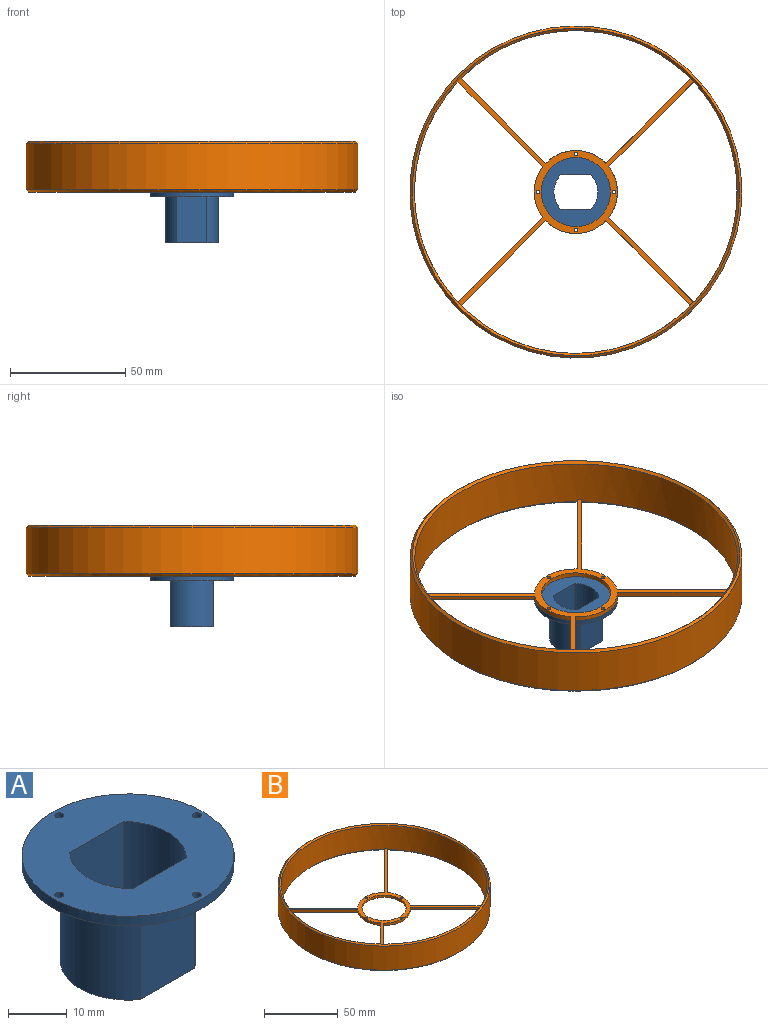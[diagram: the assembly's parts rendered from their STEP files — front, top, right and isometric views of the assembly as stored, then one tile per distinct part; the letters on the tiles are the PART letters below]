
ASSEMBLY  parts=2 mates=1
PART A: 16 faces, bbox 36x36x22 mm
  f0: plane 23x19mm, normal (0,0,-1), area 123.6mm2, adj f1,f2,f3,f8,f11,f12,f13,f14
  f1: cylinder r=10.88mm len=22mm, axis (0,0,-1), area 364.1mm2, adj f0,f2,f8,f10
  f2: plane 22x13mm, normal (0,1,0), area 286mm2, adj f0,f1,f3,f10
  f3: cylinder r=10.88mm len=22mm, axis (0,0,-1), area 364.1mm2, adj f0,f2,f8,f10
  f4: cylinder r=0.75mm len=2mm, axis (0,0,-1), area 9.4mm2, adj f10,f15
  f5: cylinder r=0.75mm len=2mm, axis (0,0,-1), area 9.4mm2, adj f10,f15
  f6: cylinder r=0.75mm len=2mm, axis (0,0,-1), area 9.4mm2, adj f10,f15
  f7: cylinder r=0.75mm len=2mm, axis (0,0,-1), area 9.4mm2, adj f10,f15
  f8: plane 22x13mm, normal (0,-1,0), area 286mm2, adj f0,f1,f3,f10
  f9: cylinder r=18mm len=36mm, axis (0,0,-1), area 226.2mm2, adj f10,f15
  f10: plane 36x36mm, normal (0,0,1), area 753.9mm2, adj f1,f2,f3,f4,f5,f6,f7,f8
  f11: plane 20x13mm, normal (0,-1,0), area 260mm2, adj f0,f12,f14,f15
  f12: cylinder r=11.53mm len=20mm, axis (0,0,-1), area 446.7mm2, adj f0,f11,f13,f15
  f13: plane 20x13mm, normal (0,1,0), area 260mm2, adj f0,f12,f14,f15
  f14: cylinder r=11.53mm len=20mm, axis (0,0,-1), area 446.7mm2, adj f0,f11,f13,f15
  f15: plane 36x36mm, normal (0,0,-1), area 630.4mm2, adj f4,f5,f6,f7,f9,f11,f12,f13
PART B: 28 faces, bbox 144x144x22 mm
  f0: cylinder r=18mm len=26.04mm, axis (0,0,-1), area 58.2mm2, adj f1,f11,f19,f20
  f1: plane 37.48x37.48mm, normal (-0.71,-0.71,0), area 104.5mm2, adj f0,f17,f19,f20,f21
  f2: plane 37.56x37.56mm, normal (-0.71,-0.71,0), area 104.7mm2, adj f3,f17,f19,f20,f22
  f3: cylinder r=18mm len=21.81mm, axis (0,0,-1), area 46.9mm2, adj f2,f4,f19,f20
  f4: plane 37.56x37.56mm, normal (-0.71,0.71,0), area 104.7mm2, adj f3,f17,f19,f20,f22
  f5: plane 37.48x37.48mm, normal (-0.71,0.71,0), area 104.5mm2, adj f6,f17,f19,f20,f23
  f6: cylinder r=18mm len=26.04mm, axis (0,0,-1), area 58.2mm2, adj f5,f7,f19,f20
  f7: plane 37.48x37.48mm, normal (0.71,0.71,0), area 104.5mm2, adj f6,f17,f19,f20,f23
  f8: plane 37.56x37.56mm, normal (0.71,0.71,0), area 104.7mm2, adj f9,f17,f19,f20,f25
  f9: cylinder r=18mm len=21.81mm, axis (0,0,-1), area 46.9mm2, adj f8,f10,f19,f20
  f10: plane 37.56x37.56mm, normal (0.71,-0.71,0), area 104.7mm2, adj f9,f17,f19,f20,f25
  f11: plane 37.48x37.48mm, normal (0.71,-0.71,0), area 104.5mm2, adj f0,f17,f19,f20,f21
  f12: cylinder r=15mm len=30mm, axis (0,0,-1), area 188.5mm2, adj f19,f20
  f13: cylinder r=0.75mm len=2mm, axis (0,0,-1), area 9.4mm2, adj f19,f20
  f14: cylinder r=0.75mm len=2mm, axis (0,0,-1), area 9.4mm2, adj f19,f20
  f15: cylinder r=0.75mm len=2mm, axis (0,0,-1), area 9.4mm2, adj f19,f20
  f16: cylinder r=0.75mm len=2mm, axis (0,0,-1), area 9.4mm2, adj f19,f20
  f17: cylinder r=70mm len=140mm, axis (0,0,-1), area 8788.5mm2, adj f1,f2,f4,f5,f7,f8,f10,f11
  f18: cylinder r=72mm len=144mm, axis (0,0,-1), area 9047.8mm2, adj f24,f27
  f19: plane 103.77x99.82mm, normal (0,0,-1), area 728.3mm2, adj f0,f1,f2,f3,f4,f5,f6,f7
  f20: plane 102.35x98.41mm, normal (0,0,1), area 720.3mm2, adj f0,f1,f2,f3,f4,f5,f6,f7
  f21: cone r=71mm half-angle=45deg, axis (0,0,-1), area 157.8mm2, adj f1,f11,f17,f24
  f22: cone r=71mm half-angle=45deg, axis (0,0,-1), area 149.8mm2, adj f2,f4,f17,f24
  f23: cone r=71mm half-angle=45deg, axis (0,0,-1), area 157.8mm2, adj f5,f7,f17,f24
  f24: cone r=72mm half-angle=45deg, axis (0,0,1), area 635.3mm2, adj f18,f19,f21,f22,f23,f25
  f25: cone r=71mm half-angle=45deg, axis (0,0,-1), area 149.8mm2, adj f8,f10,f17,f24
  f26: cone r=70mm half-angle=45deg, axis (0,0,1), area 626.4mm2, adj f17,f27
  f27: cone r=71mm half-angle=45deg, axis (0,0,-1), area 635.3mm2, adj f18,f26
PLACE A t=(1.25,7.41,-22.97)mm
PLACE B t=(1.25,7.41,-0.97)mm
MATE planar A.f9 <-> B.f9  axis (0,0,1) through (1.25,7.41,-0.97)mm
